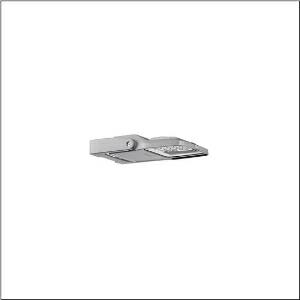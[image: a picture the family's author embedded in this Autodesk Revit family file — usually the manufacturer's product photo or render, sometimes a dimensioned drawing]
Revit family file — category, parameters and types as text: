
# Revit family: floodlight_fl_21_iq_micro___pl52_5xa7761a2d2a_1372
name_source: partatom
category: Lighting Fixtures
units: mm (PartAtom-declared; Revit-internal decimal feet)

## family parameters
Cut with Voids When Loaded = No
Host = Face
Light Source = No
Part Type = Normal
Room Calculation Point = No
Round Connector Dimension = Use Diameter
Shared = No

## types (1)
- --- (1 x LED, 2890 lm, 23.1 W, 3000K)
    Apparent Load = 23 VA
    CIE Flux Codes = 26 60 98 100 100
    Color Rendering = 70
    Color Temperature = 3000K
    Default Elevation = 1800 mm
    Description = Floodlight FL 21 iQ micro, floodlight, primary light control with lens, of PMMA, primary optical cover: protective disc, of toughened safety glass, transparent, light distribution: PL52, light emission: direct distribution, installation type: surface-mounted, LED, High Power LED, rated luminous flux: 2.890lm, luminous efficacy: 125lm/W, light colour: 730, colour temperature: 3000K, control gear: iQ Comfort/DALI, control: optimised constant luminous flux control (CLO 2.0), Desk-Remote (wireless, voltage-free reading and setting of iQ features in the workshop via application-optimized NFC function/RFID function), Light-Fading, Smart-Wire, Night-Set, Lumen-Switch, Temp-Guard, Auto-Match, with terminal, 6-pole, mains connection: 220..240V, AC, 50/60Hz, start of lifetime: 23W, end of service life: 24W, reduction: 11W, luminaire housing, of diecast aluminium, powder-coated, Siteco® metallic grey (DB 702S), corrosivity category C5 mid according to DIN EN ISO 12944, suitable for swimming pools, chlorine-resistant, sealing non-destructively replaceable, design bracket, of diecast aluminium, powder-coated, Siteco® metallic grey (DB 702S), protection rating (complete): IP66, insulation class (complete): insulation class II (safety insulation), certification: CE, ENEC, VDE, protection symbol: D, impact resistance: IK07, permissible operating ambient temperature: -40..+40°C, permissible operating ambient temperature for outdoor applications: -40..+50°C, standard: DIN EN 12944, LABS conformity tested according to VDMA 24364:2018-05, packaging unit: 1 piece

Light Distribution: PL52
    Height = 65 mm
    Lamp = 1 x LED
    Lamp Light Flux = 2890 lm
    Lamp Power = 23.1 W
    Lamp count = 1
    Length = 312 mm
    Luminous efficacy = 125 lm/W
    Manufacturer = Siteco
    ModVariant = No
    Model = 5XA7761A2D2A
    Mounting Place = Wall
    Mounting Type = Surface mounted
    Number of Poles = 1
    OnlyDefault = Yes
    Power Factor = 1
    Product Name = Floodlight FL 21 iQ micro | PL52
    Product group = floodlight | wall mounted
    ProductGroupID = 2001
    Protection Class = Protection class II
    Protection Degree = IP 66
    RLX_Detail_Level = 1
    RLX_Emergency_Light_Flux = 0 lm
    RLX_Emergency_Type = 0
    RLX_Emergency_Type_DB = No
    RlxData = <blob elided: 97693 chars, md5=70aaf643>
    Socket = socket
    Standby Power = 0 W
    System Light Flux = 2890 lm
    System Power = 23 W
    Type Comments = factory setting: luminous flux: 100 % | dim-lin: 254 | 455 mA
    Type Image = l_1006878.jpg
    URL = http://relux.com
    VarID = @adj_178134
    Voltage = 0 V
    Weight = 0.00 kg
    Width = 230 mm

## geometry (parser evidence)
native form markers: Blend x4, Sweep x12
no freeform markers — native parametric forms only
